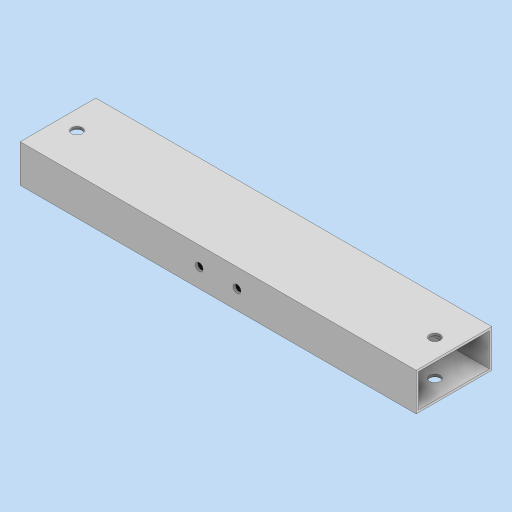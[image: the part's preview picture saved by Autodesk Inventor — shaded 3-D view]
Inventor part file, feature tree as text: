
AUTODESK INVENTOR PART (.ipt)
format: ipt  version: 2024 (Build 280153000, 153)  size: 126,976 bytes
history: native  units: in
note: dims shown in document units (in); Inventor stores cm internally (conversion verified against a paired STEP export)
features: extrude x3, sketch x3, projected_geometry x2
ambient origin geometry x8: Origin, YZ Plane, XZ Plane, XY Plane, X Axis, Y Axis, Z Axis, Center Point
bodies: Solid1 (feature_tree)
feature tree (8):
  extrude  "Extrusion1"  Depth=2.0in
  extrude  "Extrusion2"  Depth=10.4733in TaperAngle=0.0deg
  extrude  "Extrusion4"  Depth=1.0in
  sketch  "Sketch1"  dims[d0=1.0in d1=2.0in]
  sketch  "Sketch2"  dims[d2=0.0625in d3=10.4733in d4=0.0in]
  projected_geometry  "Projected Loop1"
  sketch  "Sketch4"  dims[d5=0.281in d6=0.5in d7=0.281in d9=1.0in d10=1.0in d11=1.0in d12=0.0in d21=0.203in d22=0.203in d23=0.5in d24=1.0in d25=0.0in d26=0.0in d27=0.5in d28=0.5in d29=9.469in]
  projected_geometry  "Projected Loop3"
